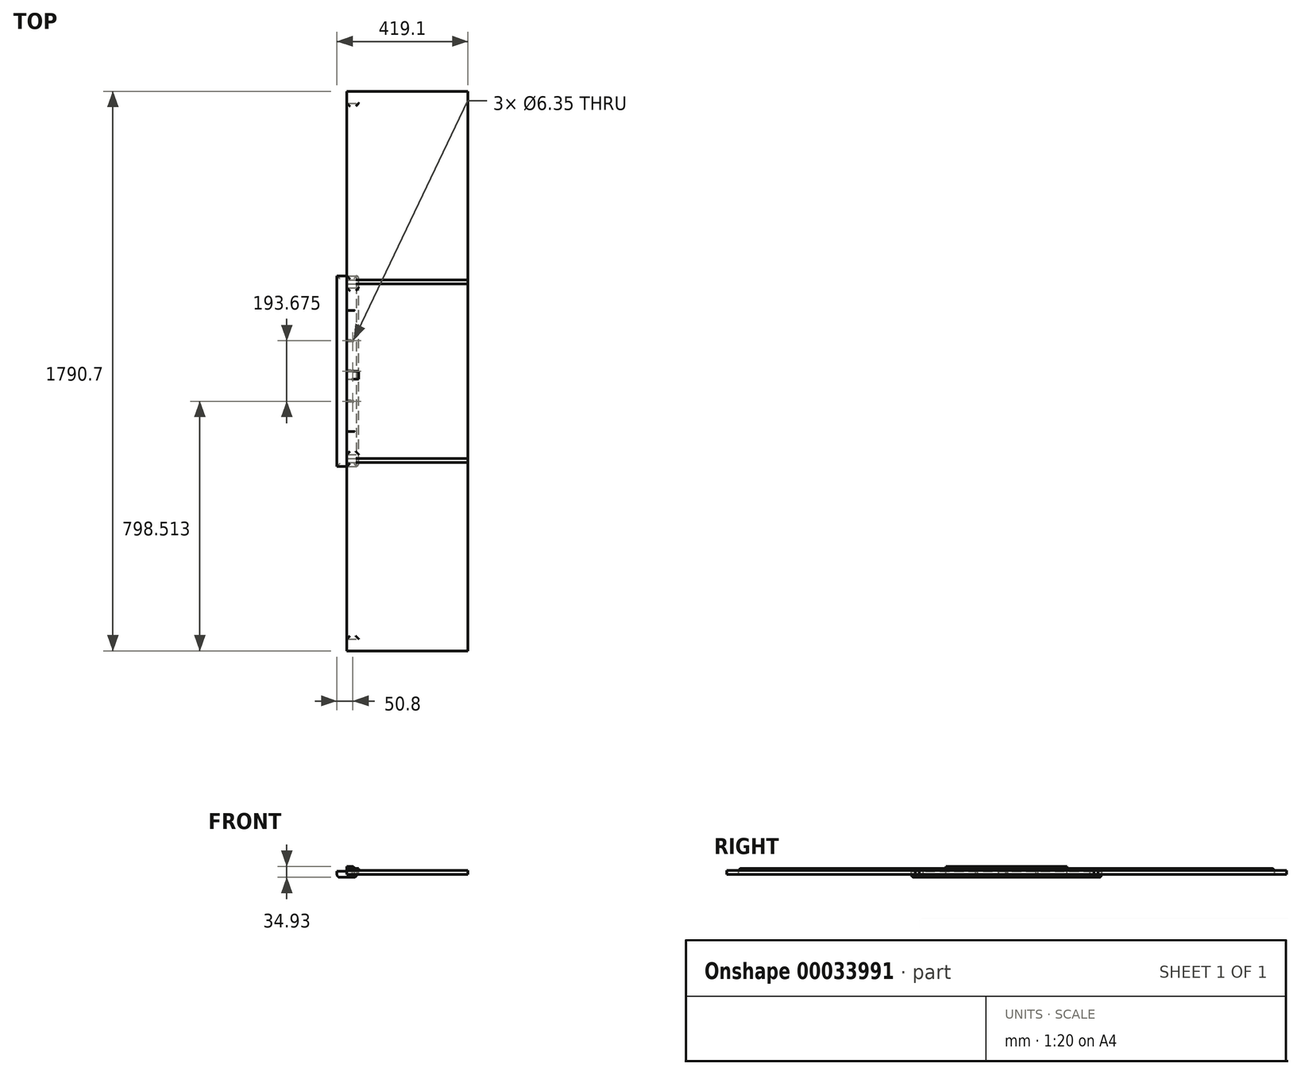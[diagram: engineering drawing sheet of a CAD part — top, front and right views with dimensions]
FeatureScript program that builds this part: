
annotation { "Feature Type Name" : "Feature", "Feature Type Description" : "" }
export const myFeature = defineFeature(function(context is Context, id is Id, definition is map)
    precondition{}
    {
        {
            var Q0;
            Q0=qCreatedBy(makeId("Front.planeOp"),FACE);
            var sketch = newSketch(context, id + "F0", { "sketchPlane" : qUnion([Q0])});
            skLineSegment(sketch, "E0.bottom", {"start": v(-31.75, 9.53) * mm, "end": v(31.75, 9.53) * mm});
            skLineSegment(sketch, "E0.top", {"start": v(-31.75, -9.52) * mm, "end": v(31.75, -9.52) * mm});
            skLineSegment(sketch, "E0.left", {"start": v(-31.75, 9.53) * mm, "end": v(-31.75, -9.52) * mm});
            skLineSegment(sketch, "E0.right", {"start": v(31.75, 9.53) * mm, "end": v(31.75, -9.52) * mm});
            skSolve(sketch);
        }
        {
            var Q0;
            Q0=makeQuery(id+"F0.imprint","IMPRINT",FACE,{"disambiguationData":[TD([[makeQuery(id+"F0.imprint","IMPRINT",EDGE,{"derivedFrom":sQuery(id+"F0.wireOp",EDGE,"E0.bottom")}),-1.0]])]});
            extrude(context, id + "F1", {"entities" : qUnion([Q0]), "endBound" : BoundingType.SYMMETRIC, "depth" : 609.6 * mm});
        }
        {
            var Q0;
            Q0=makeQuery(id+"F1.opExtrude","SWEPT_EDGE",EDGE,{"disambiguationData":[OSD([sQuery(id+"F0.wireOp",EDGE,"E0.top"),sQuery(id+"F0.wireOp",EDGE,"E0.right")])]});
            var Q1;
            Q1=makeQuery(id+"F1.opExtrude","SWEPT_EDGE",EDGE,{"disambiguationData":[OSD([sQuery(id+"F0.wireOp",EDGE,"E0.top"),sQuery(id+"F0.wireOp",EDGE,"E0.left")])]});
            var Q2;
            Q2=makeQuery(id+"F1.opExtrude","CAP_EDGE",EDGE,{"disambiguationData":[OSD([sQuery(id+"F0.wireOp",EDGE,"E0.top")])],"isStart":false});
            var Q3;
            Q3=makeQuery(id+"F1.opExtrude","CAP_EDGE",EDGE,{"disambiguationData":[OSD([sQuery(id+"F0.wireOp",EDGE,"E0.top")])],"isStart":true});
            fillet(context, id + "F2", {"entities" : qUnion([Q0, Q1, Q2, Q3]), "radius" : 9.52 * mm, "tangentPropagation" : true, "allowEdgeOverflow" : false});
        }
        {
            var Q0;
            Q0=qCreatedBy(makeId("Front.planeOp"),FACE);
            var sketch = newSketch(context, id + "F3", { "sketchPlane" : qUnion([Q0])});
            skLineSegment(sketch, "E1.bottom", {"start": v(0, 0) * mm, "end": v(38.1, 0) * mm});
            skLineSegment(sketch, "E1.top", {"start": v(0, 19.05) * mm, "end": v(38.1, 19.05) * mm});
            skLineSegment(sketch, "E1.left", {"start": v(0, 0) * mm, "end": v(0, 19.05) * mm});
            skLineSegment(sketch, "E1.right", {"start": v(38.1, 0) * mm, "end": v(38.1, 19.05) * mm});
            skSolve(sketch);
        }
        {
            var Q0;
            Q0=makeQuery(id+"F3.imprint","IMPRINT",FACE,{"disambiguationData":[TD([[makeQuery(id+"F3.imprint","IMPRINT",EDGE,{"derivedFrom":sQuery(id+"F3.wireOp",EDGE,"E1.bottom")}),1.0]])]});
            extrude(context, id + "F4", {"entities" : qUnion([Q0]), "endBound" : BoundingType.SYMMETRIC, "depth" : 609.6 * mm});
        }
        {
            var Q0;
            Q0=makeQuery(id+"F4.opExtrude","SWEPT_EDGE",EDGE,{"disambiguationData":[OSD([sQuery(id+"F3.wireOp",EDGE,"E1.top"),sQuery(id+"F3.wireOp",EDGE,"E1.right")])]});
            var Q1;
            Q1=makeQuery(id+"F4.opExtrude","SWEPT_EDGE",EDGE,{"disambiguationData":[OSD([sQuery(id+"F3.wireOp",EDGE,"E1.top"),sQuery(id+"F3.wireOp",EDGE,"E1.left")])]});
            var Q2;
            Q2=makeQuery(id+"F4.opExtrude","CAP_EDGE",EDGE,{"disambiguationData":[OSD([sQuery(id+"F3.wireOp",EDGE,"E1.top")])],"isStart":false});
            var Q3;
            Q3=makeQuery(id+"F4.opExtrude","CAP_EDGE",EDGE,{"disambiguationData":[OSD([sQuery(id+"F3.wireOp",EDGE,"E1.top")])],"isStart":true});
            fillet(context, id + "F5", {"entities" : qUnion([Q0, Q1, Q2, Q3]), "radius" : 9.52 * mm, "tangentPropagation" : true, "allowEdgeOverflow" : false});
        }
        {
            var Q0;
            Q0=qCreatedBy(makeId("Front.planeOp"),FACE);
            var sketch = newSketch(context, id + "F6", { "sketchPlane" : qUnion([Q0])});
            skLineSegment(sketch, "E2.bottom", {"start": v(0, 0) * mm, "end": v(38.1, 0) * mm});
            skLineSegment(sketch, "E2.top", {"start": v(0, 19.05) * mm, "end": v(38.1, 19.05) * mm});
            skLineSegment(sketch, "E2.left", {"start": v(0, 0) * mm, "end": v(0, 19.05) * mm});
            skLineSegment(sketch, "E2.right", {"start": v(38.1, 0) * mm, "end": v(38.1, 19.05) * mm});
            skSolve(sketch);
        }
        {
            var Q0;
            Q0=makeQuery(id+"F6.imprint","IMPRINT",FACE,{"disambiguationData":[TD([[makeQuery(id+"F6.imprint","IMPRINT",EDGE,{"derivedFrom":sQuery(id+"F6.wireOp",EDGE,"E2.bottom")}),1.0]])]});
            extrude(context, id + "F7", {"entities" : qUnion([Q0]), "endBound" : BoundingType.SYMMETRIC, "depth" : 1714.5 * mm});
        }
        {
            var Q0;
            Q0=makeQuery(id+"F7.opExtrude","SWEPT_EDGE",EDGE,{"disambiguationData":[OSD([sQuery(id+"F6.wireOp",EDGE,"E2.top"),sQuery(id+"F6.wireOp",EDGE,"E2.right")])]});
            var Q1;
            Q1=makeQuery(id+"F7.opExtrude","SWEPT_EDGE",EDGE,{"disambiguationData":[OSD([sQuery(id+"F6.wireOp",EDGE,"E2.top"),sQuery(id+"F6.wireOp",EDGE,"E2.left")])]});
            var Q2;
            Q2=makeQuery(id+"F7.opExtrude","CAP_EDGE",EDGE,{"disambiguationData":[OSD([sQuery(id+"F6.wireOp",EDGE,"E2.top")])],"isStart":false});
            var Q3;
            Q3=makeQuery(id+"F7.opExtrude","CAP_EDGE",EDGE,{"disambiguationData":[OSD([sQuery(id+"F6.wireOp",EDGE,"E2.top")])],"isStart":true});
            fillet(context, id + "F8", {"entities" : qUnion([Q0, Q1, Q2, Q3]), "radius" : 9.52 * mm, "tangentPropagation" : true, "allowEdgeOverflow" : false});
        }
        {
            var Q0;
            Q0=qCreatedBy(makeId("Front.planeOp"),FACE);
            var sketch = newSketch(context, id + "F9", { "sketchPlane" : qUnion([Q0])});
            skLineSegment(sketch, "E3.bottom", {"start": v(0, 0) * mm, "end": v(38.1, 0) * mm});
            skLineSegment(sketch, "E3.top", {"start": v(0, 19.05) * mm, "end": v(38.1, 19.05) * mm});
            skLineSegment(sketch, "E3.left", {"start": v(0, 0) * mm, "end": v(0, 19.05) * mm});
            skLineSegment(sketch, "E3.right", {"start": v(38.1, 0) * mm, "end": v(38.1, 19.05) * mm});
            skSolve(sketch);
        }
        {
            var Q0;
            Q0=makeQuery(id+"F9.imprint","IMPRINT",FACE,{"disambiguationData":[TD([[makeQuery(id+"F9.imprint","IMPRINT",EDGE,{"derivedFrom":sQuery(id+"F9.wireOp",EDGE,"E3.bottom")}),1.0]])]});
            extrude(context, id + "F10", {"entities" : qUnion([Q0]), "endBound" : BoundingType.SYMMETRIC, "depth" : 533.4 * mm});
        }
        {
            var Q0;
            Q0=makeQuery(id+"F10.opExtrude","SWEPT_EDGE",EDGE,{"disambiguationData":[OSD([sQuery(id+"F9.wireOp",EDGE,"E3.top"),sQuery(id+"F9.wireOp",EDGE,"E3.right")])]});
            var Q1;
            Q1=makeQuery(id+"F10.opExtrude","SWEPT_EDGE",EDGE,{"disambiguationData":[OSD([sQuery(id+"F9.wireOp",EDGE,"E3.top"),sQuery(id+"F9.wireOp",EDGE,"E3.left")])]});
            var Q2;
            Q2=makeQuery(id+"F10.opExtrude","CAP_EDGE",EDGE,{"disambiguationData":[OSD([sQuery(id+"F9.wireOp",EDGE,"E3.top")])],"isStart":false});
            var Q3;
            Q3=makeQuery(id+"F10.opExtrude","CAP_EDGE",EDGE,{"disambiguationData":[OSD([sQuery(id+"F9.wireOp",EDGE,"E3.top")])],"isStart":true});
            fillet(context, id + "F11", {"entities" : qUnion([Q0, Q1, Q2, Q3]), "radius" : 9.52 * mm, "tangentPropagation" : true, "allowEdgeOverflow" : false});
        }
        {
            var Q0;
            Q0=makeQuery(id+"F9.imprint","IMPRINT",FACE,{"disambiguationData":[TD([[makeQuery(id+"F9.imprint","IMPRINT",EDGE,{"derivedFrom":sQuery(id+"F9.wireOp",EDGE,"E3.bottom")}),1.0]])]});
            extrude(context, id + "F12", {"entities" : qUnion([Q0]), "depth" : 25.4 * mm});
        }
        {
            var Q0;
            Q0=qCreatedBy(makeId("Front.planeOp"),FACE);
            var sketch = newSketch(context, id + "F13", { "sketchPlane" : qUnion([Q0])});
            skLineSegment(sketch, "E4.bottom", {"start": v(0, 0) * mm, "end": v(25.4, 0) * mm});
            skLineSegment(sketch, "E4.top", {"start": v(0, 25.4) * mm, "end": v(25.4, 25.4) * mm});
            skLineSegment(sketch, "E4.left", {"start": v(0, 0) * mm, "end": v(0, 25.4) * mm});
            skLineSegment(sketch, "E4.right", {"start": v(25.4, 0) * mm, "end": v(25.4, 25.4) * mm});
            skSolve(sketch);
        }
        {
            var Q0;
            Q0=makeQuery(id+"F13.imprint","IMPRINT",FACE,{"disambiguationData":[TD([[makeQuery(id+"F13.imprint","IMPRINT",EDGE,{"derivedFrom":sQuery(id+"F13.wireOp",EDGE,"E4.bottom")}),1.0]])]});
            extrude(context, id + "F14", {"entities" : qUnion([Q0]), "endBound" : BoundingType.SYMMETRIC, "depth" : 387.35 * mm});
        }
        {
            var Q0;
            Q0=makeQuery(id+"F14.opExtrude","SWEPT_EDGE",EDGE,{"disambiguationData":[OSD([sQuery(id+"F13.wireOp",EDGE,"E4.top"),sQuery(id+"F13.wireOp",EDGE,"E4.right")])]});
            fillet(context, id + "F15", {"entities" : qUnion([Q0]), "radius" : 9.52 * mm, "tangentPropagation" : true, "allowEdgeOverflow" : false});
        }
        {
            var Q0;
            Q0=makeQuery(id+"F14.opExtrude","SWEPT_FACE",FACE,{"disambiguationData":[OSD([sQuery(id+"F13.wireOp",EDGE,"E4.left")])]});
            var sketch = newSketch(context, id + "F16", { "sketchPlane" : qUnion([Q0])});
            skPoint(sketch, "E5", {"position": v(96.84, 19.05) * mm});
            skPoint(sketch, "E6", {"position": v(0, 19.05) * mm});
            skPoint(sketch, "E7", {"position": v(-96.84, 19.05) * mm});
            skSolve(sketch);
        }
        {
            var Q0;
            Q0=sQuery(id+"F16.wireOp",VERTEX,"E7");
            var Q1;
            Q1=sQuery(id+"F16.wireOp",VERTEX,"E6");
            var Q2;
            Q2=sQuery(id+"F16.wireOp",VERTEX,"E5");
            var Q3;
            Q3=makeQuery(id+"F14.opExtrude","SWEPT_BODY",BODY,{"disambiguationData":[OSD([sQuery(id+"F13.wireOp",EDGE,"E4.bottom"),sQuery(id+"F13.wireOp",EDGE,"E4.top"),sQuery(id+"F13.wireOp",EDGE,"E4.left"),sQuery(id+"F13.wireOp",EDGE,"E4.right")])]});
            hole(context, id + "F17", {"style" : HoleStyle.SIMPLE, "holeDiameter" : 6.35 * mm, "endStyle" : HoleEndStyle.BLIND, "holeDepth" : 12.7 * mm, "locations" : qUnion([Q0, Q1, Q2]), "scope" : qUnion([Q3])});
        }
        {
            var Q0;
            Q0=makeQuery(id+"F14.opExtrude","SWEPT_FACE",FACE,{"disambiguationData":[OSD([sQuery(id+"F13.wireOp",EDGE,"E4.bottom")])]});
            var sketch = newSketch(context, id + "F18", { "sketchPlane" : qUnion([Q0])});
            skPoint(sketch, "E8", {"position": v(19.05, 96.84) * mm});
            skPoint(sketch, "E9", {"position": v(19.05, 0) * mm});
            skPoint(sketch, "E10", {"position": v(19.05, -96.84) * mm});
            skSolve(sketch);
        }
        {
            var Q0;
            Q0=sQuery(id+"F18.wireOp",VERTEX,"E8");
            var Q1;
            Q1=sQuery(id+"F18.wireOp",VERTEX,"E9");
            var Q2;
            Q2=sQuery(id+"F18.wireOp",VERTEX,"E10");
            var Q3;
            Q3=makeQuery(id+"F14.opExtrude","SWEPT_BODY",BODY,{"disambiguationData":[OSD([sQuery(id+"F13.wireOp",EDGE,"E4.bottom"),sQuery(id+"F13.wireOp",EDGE,"E4.top"),sQuery(id+"F13.wireOp",EDGE,"E4.left"),sQuery(id+"F13.wireOp",EDGE,"E4.right")])]});
            hole(context, id + "F19", {"style" : HoleStyle.SIMPLE, "holeDiameter" : 6.35 * mm, "endStyle" : HoleEndStyle.BLIND, "holeDepth" : 12.7 * mm, "locations" : qUnion([Q0, Q1, Q2]), "scope" : qUnion([Q3])});
        }
        {
            var Q0;
            Q0=makeQuery(id+"F4.opExtrude","CAP_EDGE",EDGE,{"disambiguationData":[OSD([sQuery(id+"F3.wireOp",EDGE,"E1.right")])],"isStart":false});
            var Q1;
            Q1=makeQuery(id+"F4.opExtrude","CAP_EDGE",EDGE,{"disambiguationData":[OSD([sQuery(id+"F3.wireOp",EDGE,"E1.right")])],"isStart":true});
            fillet(context, id + "F20", {"entities" : qUnion([Q0, Q1]), "radius" : 9.52 * mm, "tangentPropagation" : true, "allowEdgeOverflow" : false});
        }
        {
            var Q0;
            Q0=qCreatedBy(makeId("Front.planeOp"),FACE);
            var sketch = newSketch(context, id + "F21", { "sketchPlane" : qUnion([Q0])});
            skLineSegment(sketch, "E11.bottom", {"start": v(0, 0) * mm, "end": v(387.35, 0) * mm});
            skLineSegment(sketch, "E11.top", {"start": v(0, 12.7) * mm, "end": v(387.35, 12.7) * mm});
            skLineSegment(sketch, "E11.left", {"start": v(0, 0) * mm, "end": v(0, 12.7) * mm});
            skLineSegment(sketch, "E11.right", {"start": v(387.35, 0) * mm, "end": v(387.35, 12.7) * mm});
            skSolve(sketch);
        }
        {
            var Q0;
            Q0=makeQuery(id+"F21.imprint","IMPRINT",FACE,{"disambiguationData":[TD([[makeQuery(id+"F21.imprint","IMPRINT",EDGE,{"derivedFrom":sQuery(id+"F21.wireOp",EDGE,"E11.bottom")}),1.0]])]});
            extrude(context, id + "F22", {"entities" : qUnion([Q0]), "endBound" : BoundingType.SYMMETRIC, "depth" : 558.8 * mm});
        }
        {
            var Q0;
            Q0=qCreatedBy(makeId("Front.planeOp"),FACE);
            var sketch = newSketch(context, id + "F23", { "sketchPlane" : qUnion([Q0])});
            skLineSegment(sketch, "E12.bottom", {"start": v(0, 0) * mm, "end": v(387.35, 0) * mm});
            skLineSegment(sketch, "E12.top", {"start": v(0, 12.7) * mm, "end": v(387.35, 12.7) * mm});
            skLineSegment(sketch, "E12.left", {"start": v(0, 0) * mm, "end": v(0, 12.7) * mm});
            skLineSegment(sketch, "E12.right", {"start": v(387.35, 0) * mm, "end": v(387.35, 12.7) * mm});
            skSolve(sketch);
        }
        {
            var Q0;
            Q0=makeQuery(id+"F23.imprint","IMPRINT",FACE,{"disambiguationData":[TD([[makeQuery(id+"F23.imprint","IMPRINT",EDGE,{"derivedFrom":sQuery(id+"F23.wireOp",EDGE,"E12.bottom")}),1.0]])]});
            extrude(context, id + "F24", {"entities" : qUnion([Q0]), "endBound" : BoundingType.SYMMETRIC, "depth" : 1790.7 * mm});
        }
        {
            var Q0;
            Q0=qCreatedBy(makeId("Front.planeOp"),FACE);
            var sketch = newSketch(context, id + "F25", { "sketchPlane" : qUnion([Q0])});
            skPoint(sketch, "E13.0", {"position": v(0, 0) * mm});
            skLineSegment(sketch, "E14.bottom", {"start": v(0, 0) * mm, "end": v(387.35, 0) * mm});
            skLineSegment(sketch, "E14.top", {"start": v(0, 12.7) * mm, "end": v(387.35, 12.7) * mm});
            skLineSegment(sketch, "E14.left", {"start": v(0, 0) * mm, "end": v(0, 12.7) * mm});
            skLineSegment(sketch, "E14.right", {"start": v(387.35, 0) * mm, "end": v(387.35, 12.7) * mm});
            skSolve(sketch);
        }
        {
            var Q0;
            Q0=makeQuery(id+"F25.imprint","IMPRINT",FACE,{"disambiguationData":[TD([[makeQuery(id+"F25.imprint","IMPRINT",EDGE,{"derivedFrom":sQuery(id+"F25.wireOp",EDGE,"E14.bottom")}),1.0]])]});
            extrude(context, id + "F26", {"entities" : qUnion([Q0]), "endBound" : BoundingType.SYMMETRIC, "depth" : 584.2 * mm});
        }
    });
